# Revit family: P191568KX-117c_KFGD500E
name_source: partatom
category: Specialty Equipment
units: mm (PartAtom-declared; Revit-internal decimal feet)

## family parameters
Always vertical = Yes
Cut with Voids When Loaded = No
Enable Cutting in Views = No
Maintain Annotation Orientation = No
Part Type = Normal
Room Calculation Point = No
Round Connector Dimension = Use Diameter
Shared = No
Work Plane-Based = No

## types (1)
- KFGD500ESS
    Amps = 0 A
    Body Material = ARCAT - Metal - Steel - Stainless
    Clearance Material = ARCAT - Clearance
    Cooking Grate Material = ARCAT - Metal - Cast Iron 1/4" Plate
    Default Elevation = 0"
    Depth = 28 1/2"
    Description = 30-Inch 5 Burner Gas Double Oven Convection Range
Cuisinière au gaz avec 5 éléments et four double à convection, 30 po
    Dimension Guide = https://www.whirlpool.com
https://www.whirlpool.com
    Display Panel Material = ARCAT - Glass - Black
    Door Material = ARCAT - Metal - Steel - Stainless
    Family Name = COOKING
    Feature 1 = Even-Heat™ True Convection
Convection véritable Even-Heat™
    Feature 2 = 6.0 Cu. Ft. Total Capacity
Capacité totale de 6 pi cu
    Feature 3 = Professionally-Inspired Design
Conception d'inspiration professionnelle
    Glass Material = ARCAT - Glass - Tempered - Black
    Handle Material = ARCAT - Metal - Steel - Stainless
    Height = 47 3/8"
    Installation-Fabrication = http://access.whirlpool.com Instruction&sku=KFGD500EBS&language=EN
http://access.whirlpool.com Instruction&sku=KFGD500EBS&language=FR
    Knob Material = ARCAT - Metal - Steel - Gray
    Leg Material = ARCAT - Plastic - Black
    Manufacturer = KitchenAid
    Model = KFGD500ESS
    Voltage = 0 V
    Width = 29 15/16"

## geometry (parser evidence)
native form markers: Sweep x6
no freeform markers — native parametric forms only
